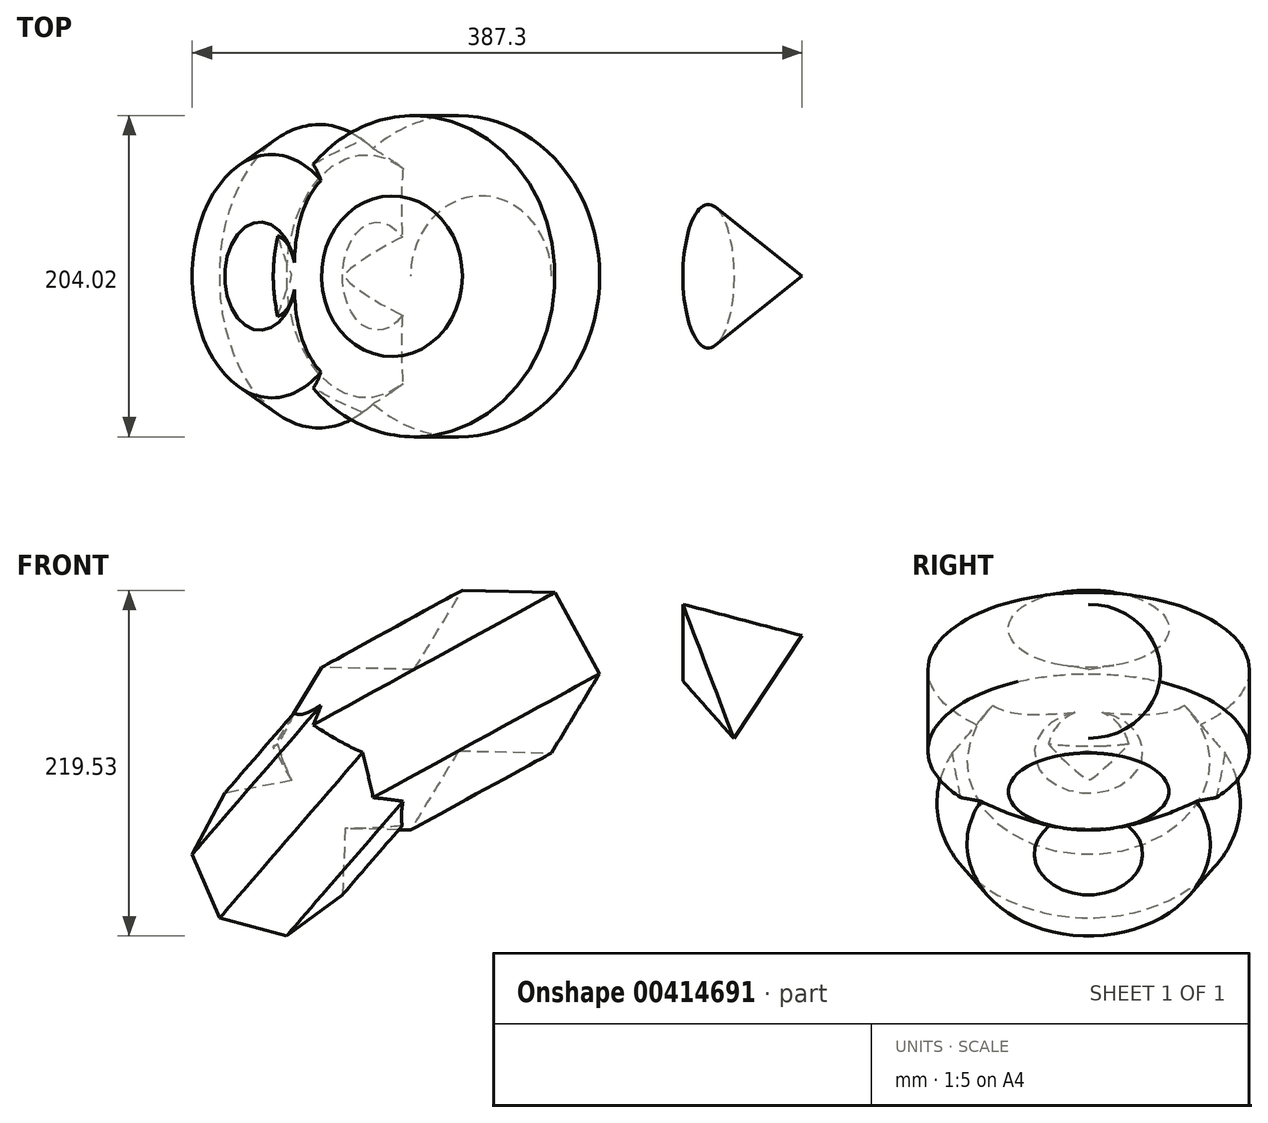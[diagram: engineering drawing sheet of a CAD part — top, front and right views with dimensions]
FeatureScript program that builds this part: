
annotation { "Feature Type Name" : "Feature", "Feature Type Description" : "" }
export const myFeature = defineFeature(function(context is Context, id is Id, definition is map)
    precondition{}
    {
        {
            var Q0;
            Q0=qCreatedBy(makeId("Front.planeOp"),FACE);
            var sketch = newSketch(context, id + "F0", { "sketchPlane" : qUnion([Q0])});
            skCircle(sketch, "E0.cCircle", {"center": v(0, 0) * mm, "radius": 51 * mm, "construction": true});
            skLineSegment(sketch, "E0.0", {"start": v(30.6, 50.32) * mm, "end": v(58.88, -1.34) * mm});
            skLineSegment(sketch, "E0.1", {"start": v(58.88, -1.34) * mm, "end": v(28.28, -51.67) * mm});
            skLineSegment(sketch, "E0.2", {"start": v(28.28, -51.67) * mm, "end": v(-30.6, -50.32) * mm});
            skLineSegment(sketch, "E0.3", {"start": v(-30.6, -50.32) * mm, "end": v(-58.88, 1.34) * mm});
            skLineSegment(sketch, "E0.4", {"start": v(-58.88, 1.34) * mm, "end": v(-28.28, 51.67) * mm});
            skLineSegment(sketch, "E0.5", {"start": v(-28.28, 51.67) * mm, "end": v(30.6, 50.32) * mm});
            skPoint(sketch, "E0.0.midPoint", {"position": v(44.74, 24.49) * mm});
            skSolve(sketch);
        }
        {
            var Q0;
            Q0 = qSketchRegion(id + "F0", true);
            var Q1;
            Q1=sQuery(id+"F0.wireOp",EDGE,"E0.0");
            revolve(context, id + "F1", {"entities" : qUnion([Q0]), "axis" : qUnion([Q1]), "revolveType" : RevolveType.FULL});
        }
        {
            var Q0;
            Q0=qCreatedBy(makeId("Front.planeOp"),FACE);
            var sketch = newSketch(context, id + "F2", { "sketchPlane" : qUnion([Q0])});
            skCircle(sketch, "E1.cCircle", {"center": v(0, 0) * mm, "radius": 45.66 * mm, "construction": true});
            skLineSegment(sketch, "E1.0", {"start": v(33.15, 38.33) * mm, "end": v(50.64, -2.02) * mm});
            skLineSegment(sketch, "E1.1", {"start": v(50.64, -2.02) * mm, "end": v(30, -40.85) * mm});
            skLineSegment(sketch, "E1.2", {"start": v(30, -40.85) * mm, "end": v(-13.24, -48.92) * mm});
            skLineSegment(sketch, "E1.3", {"start": v(-13.24, -48.92) * mm, "end": v(-46.5, -20.15) * mm});
            skLineSegment(sketch, "E1.4", {"start": v(-46.5, -20.15) * mm, "end": v(-44.75, 23.8) * mm});
            skLineSegment(sketch, "E1.5", {"start": v(-44.75, 23.8) * mm, "end": v(-9.3, 49.82) * mm});
            skLineSegment(sketch, "E1.6", {"start": v(-9.3, 49.82) * mm, "end": v(33.15, 38.33) * mm});
            skPoint(sketch, "E1.0.midPoint", {"position": v(41.9, 18.16) * mm});
            skSolve(sketch);
        }
        {
            var Q0;
            Q0 = qSketchRegion(id + "F2", true);
            var Q1;
            Q1=sQuery(id+"F2.wireOp",EDGE,"E1.3");
            revolve(context, id + "F3", {"operationType" : NewBodyOperationType.ADD, "entities" : qUnion([Q0]), "axis" : qUnion([Q1]), "revolveType" : RevolveType.FULL});
        }
        {
            var Q0;
            Q0=qCreatedBy(makeId("Front.planeOp"),FACE);
            var sketch = newSketch(context, id + "F4", { "sketchPlane" : qUnion([Q0])});
            skLineSegment(sketch, "E2", {"start": v(201.23, 91.8) * mm, "end": v(201.23, 43.07) * mm});
            skLineSegment(sketch, "E3", {"start": v(201.23, 43.07) * mm, "end": v(276.93, 71.84) * mm});
            skLineSegment(sketch, "E4", {"start": v(276.93, 71.84) * mm, "end": v(201.23, 91.8) * mm});
            skSolve(sketch);
        }
        {
            var Q0;
            Q0 = qSketchRegion(id + "F4", true);
            var Q1;
            Q1=sQuery(id+"F4.wireOp",EDGE,"E3");
            revolve(context, id + "F5", {"entities" : qUnion([Q0]), "axis" : qUnion([Q1]), "revolveType" : RevolveType.FULL});
        }
    });
